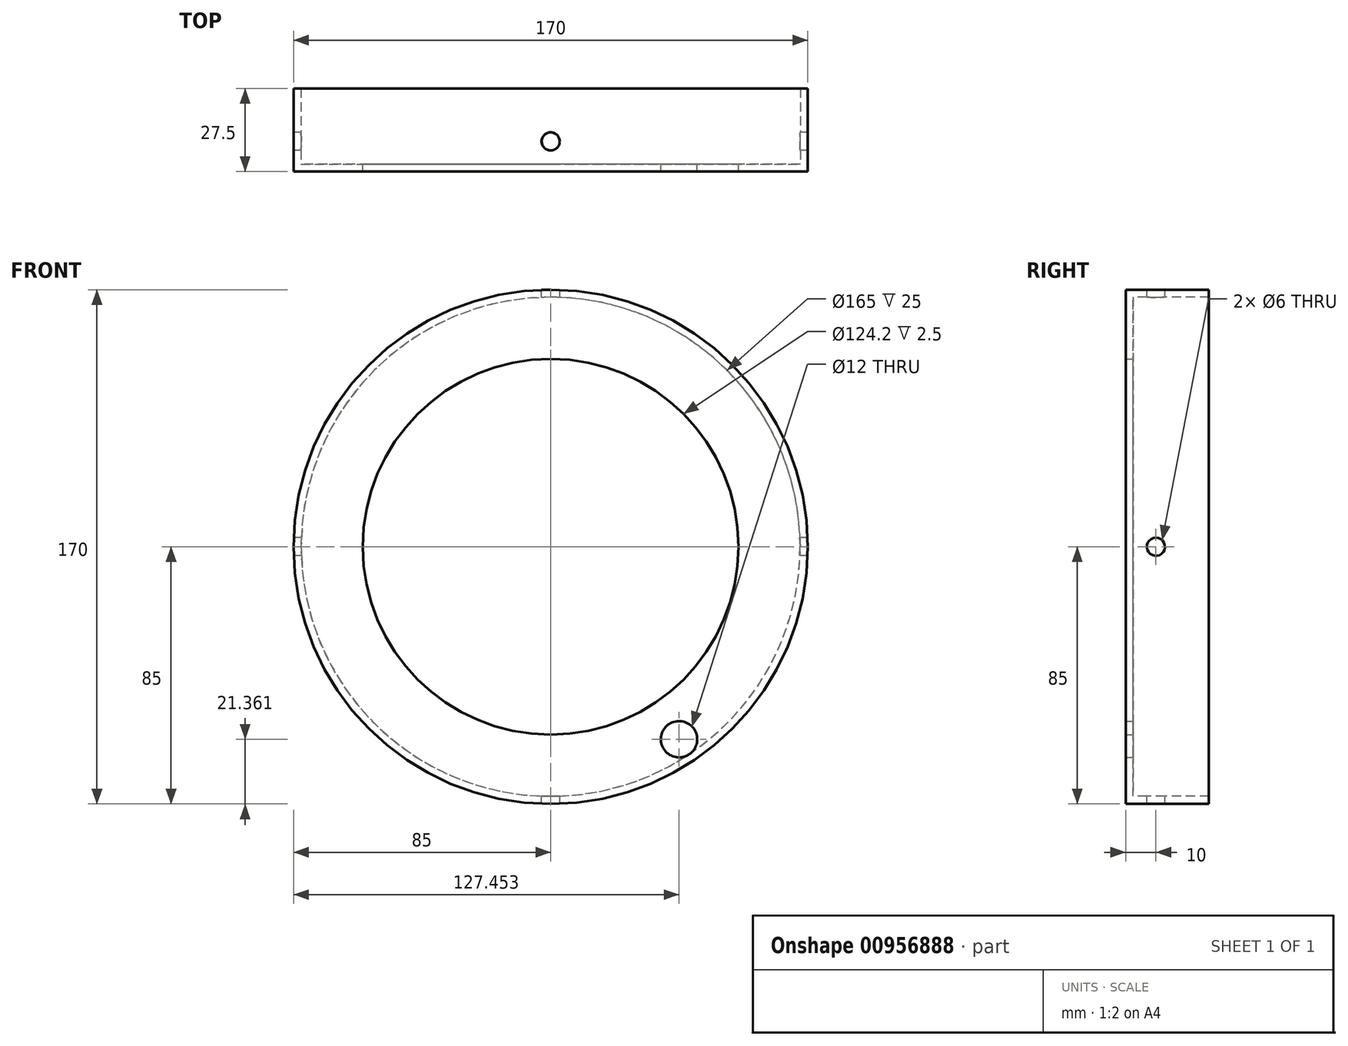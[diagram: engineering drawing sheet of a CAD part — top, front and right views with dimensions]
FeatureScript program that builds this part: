
annotation { "Feature Type Name" : "Feature", "Feature Type Description" : "" }
export const myFeature = defineFeature(function(context is Context, id is Id, definition is map)
    precondition{}
    {
        {
            var Q0;
            Q0=qCreatedBy(makeId("Front.planeOp"),FACE);
            var sketch = newSketch(context, id + "F0", { "sketchPlane" : qUnion([Q0])});
            skCircle(sketch, "E0", {"center": v(0, 0) * mm, "radius": 85 * mm});
            skCircle(sketch, "E1", {"center": v(0, 0) * mm, "radius": 62.1 * mm});
            skSolve(sketch);
        }
        {
            var Q0;
            Q0=makeQuery(id+"F0.imprint","IMPRINT",FACE,{"disambiguationData":[TD([[makeQuery(id+"F0.imprint","IMPRINT",EDGE,{"derivedFrom":sQuery(id+"F0.wireOp",EDGE,"E0")}),1.0]])]});
            extrude(context, id + "F1", {"entities" : qUnion([Q0]), "depth" : 2.5 * mm, "offsetDistance" : 25 * mm});
        }
        {
            var Q0;
            Q0=makeQuery(id+"F1.opExtrude","CAP_FACE",FACE,{"disambiguationData":[OSD([sQuery(id+"F0.wireOp",EDGE,"E0"),sQuery(id+"F0.wireOp",EDGE,"E1")])],"isStart":true});
            var sketch = newSketch(context, id + "F2", { "sketchPlane" : qUnion([Q0])});
            skCircle(sketch, "E2", {"center": v(0, 0) * mm, "radius": 82.5 * mm});
            skSolve(sketch);
        }
        {
            var Q0;
            Q0=makeQuery(id+"F2.imprint","IMPRINT",FACE,{"disambiguationData":[TD([[makeQuery(id+"F2.imprint","IMPRINT",EDGE,{"derivedFrom":sQuery(id+"F2.wireOp",EDGE,"E2")}),-1.0]])]});
            extrude(context, id + "F3", {"entities" : qUnion([Q0]), "operationType" : NewBodyOperationType.ADD, "depth" : 25 * mm, "offsetDistance" : 25 * mm});
        }
        {
            var Q0;
            Q0=qCreatedBy(makeId("Top.planeOp"),FACE);
            var sketch = newSketch(context, id + "F4", { "sketchPlane" : qUnion([Q0])});
            skCircle(sketch, "E3", {"center": v(0, 7.5) * mm, "radius": 3 * mm});
            skSolve(sketch);
        }
        {
            var Q0;
            Q0 = qSketchRegion(id + "F4", true);
            extrude(context, id + "F5", {"entities" : qUnion([Q0]), "operationType" : NewBodyOperationType.REMOVE, "endBound" : BoundingType.THROUGH_ALL, "oppositeDirection" : true, "depth" : 25 * mm, "offsetDistance" : 25 * mm, "hasSecondDirection" : true, "secondDirectionBound" : SecondDirectionBoundingType.THROUGH_ALL, "secondDirectionOppositeDirection" : false, "secondDirectionDepth" : 25 * mm});
        }
        {
            var Q0;
            Q0=qCreatedBy(makeId("Right.planeOp"),FACE);
            var sketch = newSketch(context, id + "F6", { "sketchPlane" : qUnion([Q0])});
            skCircle(sketch, "E4", {"center": v(7.5, 0) * mm, "radius": 3 * mm});
            skSolve(sketch);
        }
        {
            var Q0;
            Q0 = qSketchRegion(id + "F6", true);
            extrude(context, id + "F7", {"entities" : qUnion([Q0]), "operationType" : NewBodyOperationType.REMOVE, "endBound" : BoundingType.THROUGH_ALL, "depth" : 25 * mm, "offsetDistance" : 25 * mm, "hasSecondDirection" : true, "secondDirectionBound" : SecondDirectionBoundingType.THROUGH_ALL, "secondDirectionOppositeDirection" : true, "secondDirectionDepth" : 25 * mm});
        }
        {
            var Q0;
            Q0=qCreatedBy(makeId("Front.planeOp"),FACE);
            var sketch = newSketch(context, id + "F8", { "sketchPlane" : qUnion([Q0])});
            skCircle(sketch, "E5", {"center": v(42.45, -63.64) * mm, "radius": 6 * mm});
            skSolve(sketch);
        }
        {
            var Q0;
            Q0 = qSketchRegion(id + "F8", true);
            extrude(context, id + "F9", {"entities" : qUnion([Q0]), "operationType" : NewBodyOperationType.REMOVE, "depth" : 25 * mm, "offsetDistance" : 25 * mm});
        }
    });
